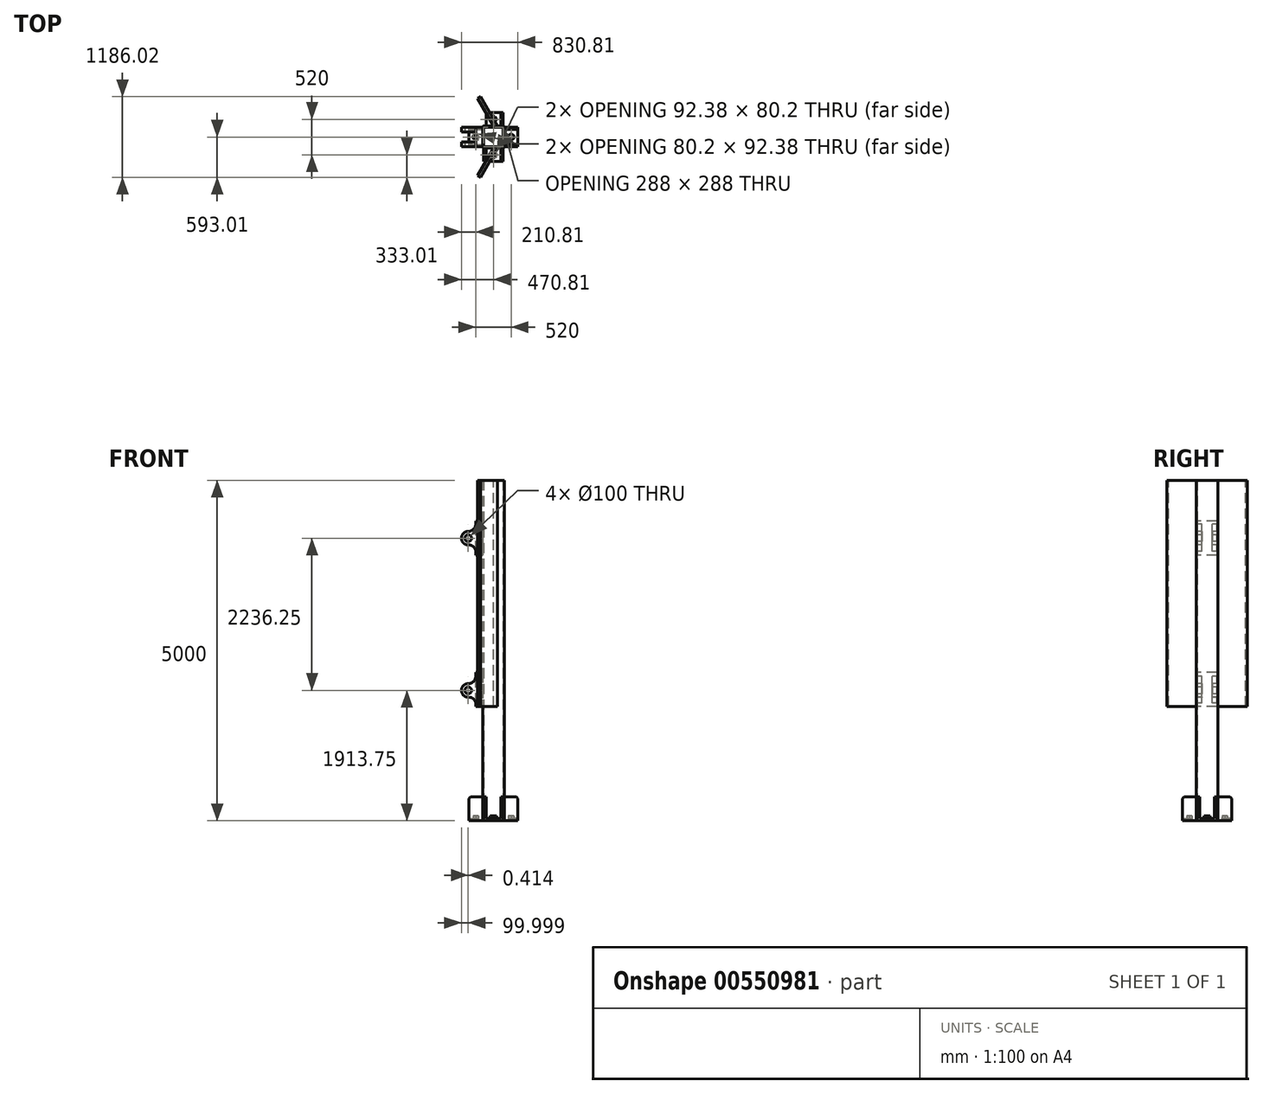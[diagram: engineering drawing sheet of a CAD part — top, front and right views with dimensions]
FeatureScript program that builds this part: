
annotation { "Feature Type Name" : "Feature", "Feature Type Description" : "" }
export const myFeature = defineFeature(function(context is Context, id is Id, definition is map)
    precondition{}
    {
        {
            var Q0;
            Q0=qCreatedBy(makeId("Top.planeOp"),FACE);
            var sketch = newSketch(context, id + "F0", { "sketchPlane" : qUnion([Q0])});
            skLineSegment(sketch, "E0.bottom", {"start": v(144, -160) * mm, "end": v(-144, -160) * mm});
            skLineSegment(sketch, "E0.top", {"start": v(144, 160) * mm, "end": v(-144, 160) * mm});
            skLineSegment(sketch, "E0.left", {"start": v(160, -144) * mm, "end": v(160, 144) * mm});
            skLineSegment(sketch, "E0.right", {"start": v(-160, -144) * mm, "end": v(-160, 144) * mm});
            skPoint(sketch, "E0.middle", {"position": v(0, 0) * mm});
            skLineSegment(sketch, "E1.0", {"start": v(128, 144) * mm, "end": v(-128, 144) * mm});
            skLineSegment(sketch, "E1.1", {"start": v(144, -128) * mm, "end": v(144, 128) * mm});
            skLineSegment(sketch, "E1.2", {"start": v(128, -144) * mm, "end": v(-128, -144) * mm});
            skLineSegment(sketch, "E1.3", {"start": v(-144, -128) * mm, "end": v(-144, 128) * mm});
            skPoint(sketch, "E2.visualSharp", {"position": v(-144, 144) * mm});
            skArc(sketch, "E2.filletArc", {"start": v(-128, 144) * mm, "mid": v(-139.31, 139.31) * mm, "end": v(-144, 128) * mm});
            skPoint(sketch, "E3.visualSharp", {"position": v(-160, 160) * mm});
            skArc(sketch, "E3.filletArc", {"start": v(-144, 160) * mm, "mid": v(-155.31, 155.31) * mm, "end": v(-160, 144) * mm});
            skPoint(sketch, "E4.visualSharp", {"position": v(-160, -160) * mm});
            skArc(sketch, "E4.filletArc", {"start": v(-160, -144) * mm, "mid": v(-155.31, -155.31) * mm, "end": v(-144, -160) * mm});
            skArc(sketch, "E5.filletArc", {"start": v(-144, -128) * mm, "mid": v(-139.31, -139.31) * mm, "end": v(-128, -144) * mm});
            skPoint(sketch, "E6.visualSharp", {"position": v(144, -144) * mm});
            skArc(sketch, "E6.filletArc", {"start": v(128, -144) * mm, "mid": v(139.31, -139.31) * mm, "end": v(144, -128) * mm});
            skPoint(sketch, "E7.visualSharp", {"position": v(160, -160) * mm});
            skArc(sketch, "E7.filletArc", {"start": v(144, -160) * mm, "mid": v(155.31, -155.31) * mm, "end": v(160, -144) * mm});
            skPoint(sketch, "E8.visualSharp", {"position": v(160, 160) * mm});
            skArc(sketch, "E8.filletArc", {"start": v(160, 144) * mm, "mid": v(155.31, 155.31) * mm, "end": v(144, 160) * mm});
            skArc(sketch, "E9.filletArc", {"start": v(144, 128) * mm, "mid": v(139.31, 139.31) * mm, "end": v(128, 144) * mm});
            skLineSegment(sketch, "E10", {"start": v(0, 0) * mm, "end": v(0, 254.28) * mm, "construction": true});
            skLineSegment(sketch, "E11.0", {"start": v(46.19, 259.8) * mm, "end": v(22.92, 219.9) * mm});
            skLineSegment(sketch, "E11.1", {"start": v(22.92, 219.9) * mm, "end": v(-23.27, 220.1) * mm});
            skLineSegment(sketch, "E11.2", {"start": v(-23.27, 220.1) * mm, "end": v(-46.19, 260.2) * mm});
            skLineSegment(sketch, "E11.3", {"start": v(-46.19, 260.2) * mm, "end": v(-22.92, 300.1) * mm});
            skLineSegment(sketch, "E11.4", {"start": v(-22.92, 300.1) * mm, "end": v(23.27, 299.9) * mm});
            skLineSegment(sketch, "E11.5", {"start": v(23.27, 299.9) * mm, "end": v(46.19, 259.8) * mm});
            skPoint(sketch, "E11.0.midPoint", {"position": v(34.55, 239.85) * mm});
            skLineSegment(sketch, "E12.bottom", {"start": v(-144, 160) * mm, "end": v(-109, 160) * mm});
            skLineSegment(sketch, "E12.top", {"start": v(-144, 360) * mm, "end": v(-109, 360) * mm});
            skLineSegment(sketch, "E12.left", {"start": v(-144, 160) * mm, "end": v(-144, 360) * mm});
            skLineSegment(sketch, "E12.right", {"start": v(144, 160) * mm, "end": v(144, 360) * mm});
            skLineSegment(sketch, "E13.1.0", {"start": v(-160, -144) * mm, "end": v(-360, -144) * mm});
            skLineSegment(sketch, "E13.1.1", {"start": v(-360, -144) * mm, "end": v(-360, 144) * mm});
            skLineSegment(sketch, "E13.1.2", {"start": v(-160, 144) * mm, "end": v(-360, 144) * mm});
            skLineSegment(sketch, "E13.1.3", {"start": v(-300.1, -22.92) * mm, "end": v(-299.9, 23.27) * mm});
            skLineSegment(sketch, "E13.1.4", {"start": v(-299.9, 23.27) * mm, "end": v(-259.8, 46.19) * mm});
            skPoint(sketch, "E13.1.5", {"position": v(-239.85, 34.55) * mm});
            skLineSegment(sketch, "E13.1.6", {"start": v(-259.8, 46.19) * mm, "end": v(-219.9, 22.92) * mm});
            skLineSegment(sketch, "E13.1.7", {"start": v(-219.9, 22.92) * mm, "end": v(-220.1, -23.27) * mm});
            skLineSegment(sketch, "E13.1.8", {"start": v(-220.1, -23.27) * mm, "end": v(-260.2, -46.19) * mm});
            skLineSegment(sketch, "E13.1.9", {"start": v(-260.2, -46.19) * mm, "end": v(-300.1, -22.92) * mm});
            skLineSegment(sketch, "E13.2.0", {"start": v(144, -160) * mm, "end": v(144, -360) * mm});
            skLineSegment(sketch, "E13.2.1", {"start": v(144, -360) * mm, "end": v(-144, -360) * mm});
            skLineSegment(sketch, "E13.2.2", {"start": v(-144, -160) * mm, "end": v(-144, -360) * mm});
            skLineSegment(sketch, "E13.2.3", {"start": v(22.92, -300.1) * mm, "end": v(-23.27, -299.9) * mm});
            skLineSegment(sketch, "E13.2.4", {"start": v(-23.27, -299.9) * mm, "end": v(-46.19, -259.8) * mm});
            skPoint(sketch, "E13.2.5", {"position": v(-34.55, -239.85) * mm});
            skLineSegment(sketch, "E13.2.6", {"start": v(-46.19, -259.8) * mm, "end": v(-22.92, -219.9) * mm});
            skLineSegment(sketch, "E13.2.7", {"start": v(-22.92, -219.9) * mm, "end": v(23.27, -220.1) * mm});
            skLineSegment(sketch, "E13.2.8", {"start": v(23.27, -220.1) * mm, "end": v(46.19, -260.2) * mm});
            skLineSegment(sketch, "E13.2.9", {"start": v(46.19, -260.2) * mm, "end": v(22.92, -300.1) * mm});
            skLineSegment(sketch, "E13.3.0", {"start": v(160, 144) * mm, "end": v(360, 144) * mm});
            skLineSegment(sketch, "E13.3.1", {"start": v(360, 144) * mm, "end": v(360, -144) * mm});
            skLineSegment(sketch, "E13.3.2", {"start": v(160, -144) * mm, "end": v(360, -144) * mm});
            skLineSegment(sketch, "E13.3.3", {"start": v(300.1, 22.92) * mm, "end": v(299.9, -23.27) * mm});
            skLineSegment(sketch, "E13.3.4", {"start": v(299.9, -23.27) * mm, "end": v(259.8, -46.19) * mm});
            skPoint(sketch, "E13.3.5", {"position": v(239.85, -34.55) * mm});
            skLineSegment(sketch, "E13.3.6", {"start": v(259.8, -46.19) * mm, "end": v(219.9, -22.92) * mm});
            skLineSegment(sketch, "E13.3.7", {"start": v(219.9, -22.92) * mm, "end": v(220.1, 23.27) * mm});
            skLineSegment(sketch, "E13.3.8", {"start": v(220.1, 23.27) * mm, "end": v(260.2, 46.19) * mm});
            skLineSegment(sketch, "E13.3.9", {"start": v(260.2, 46.19) * mm, "end": v(300.1, 22.92) * mm});
            skLineSegment(sketch, "E14", {"start": v(-109, 360) * mm, "end": v(-109, 160) * mm});
            skLineSegment(sketch, "E15", {"start": v(109, 360) * mm, "end": v(109, 160) * mm});
            skLineSegment(sketch, "E16", {"start": v(-109, 360) * mm, "end": v(109, 360) * mm});
            skLineSegment(sketch, "E17", {"start": v(109, 360) * mm, "end": v(144, 360) * mm});
            skLineSegment(sketch, "E18", {"start": v(-109, 160) * mm, "end": v(109, 160) * mm});
            skLineSegment(sketch, "E19", {"start": v(109, 160) * mm, "end": v(144, 160) * mm});
            skLineSegment(sketch, "E20.1.0", {"start": v(-360, -109) * mm, "end": v(-160, -109) * mm});
            skLineSegment(sketch, "E20.1.1", {"start": v(-360, 109) * mm, "end": v(-160, 109) * mm});
            skLineSegment(sketch, "E20.2.0", {"start": v(109, -360) * mm, "end": v(109, -160) * mm});
            skLineSegment(sketch, "E20.2.1", {"start": v(-109, -360) * mm, "end": v(-109, -160) * mm});
            skLineSegment(sketch, "E20.3.0", {"start": v(360, 109) * mm, "end": v(160, 109) * mm});
            skLineSegment(sketch, "E20.3.1", {"start": v(360, -109) * mm, "end": v(160, -109) * mm});
            skSolve(sketch);
        }
        {
            var Q0;
            Q0=makeQuery(id+"F0.imprint","IMPRINT",FACE,{"disambiguationData":[TD([[makeQuery(id+"F0.imprint","IMPRINT",EDGE,{"derivedFrom":sQuery(id+"F0.wireOp",EDGE,"E0.bottom")}),-1.0]])]});
            extrude(context, id + "F1", {"entities" : qUnion([Q0]), "depth" : 5000 * mm, "offsetDistance" : 25 * mm});
        }
        {
            var Q0;
            Q0=makeQuery(id+"F0.imprint","IMPRINT",FACE,{"disambiguationData":[TD([[makeQuery(id+"F0.imprint","IMPRINT",EDGE,{"derivedFrom":sQuery(id+"F0.wireOp",EDGE,"E14")}),1.0]])]});
            var Q1;
            {var subQ0=sQuery(id+"F0.wireOp",EDGE,"E20.3.0");Q1=makeQuery(id+"F0.imprint","IMPRINT",FACE,{"disambiguationData":[TD([[makeQuery(id+"F0.imprint","IMPRINT",EDGE,{"derivedFrom":subQ0}),1.0]])]});}
            var Q2;
            {var subQ0=sQuery(id+"F0.wireOp",EDGE,"E20.2.0");Q2=makeQuery(id+"F0.imprint","IMPRINT",FACE,{"disambiguationData":[TD([[makeQuery(id+"F0.imprint","IMPRINT",EDGE,{"derivedFrom":subQ0}),1.0]])]});}
            var Q3;
            {var subQ0=sQuery(id+"F0.wireOp",EDGE,"E20.1.0");Q3=makeQuery(id+"F0.imprint","IMPRINT",FACE,{"disambiguationData":[TD([[makeQuery(id+"F0.imprint","IMPRINT",EDGE,{"derivedFrom":subQ0}),1.0]])]});}
            extrude(context, id + "F2", {"entities" : qUnion([Q0, Q1, Q2, Q3]), "operationType" : NewBodyOperationType.ADD, "depth" : 35 * mm, "offsetDistance" : 25 * mm});
        }
        {
            var Q0;
            Q0=makeQuery(id+"F0.imprint","IMPRINT",FACE,{"disambiguationData":[TD([[makeQuery(id+"F0.imprint","IMPRINT",EDGE,{"derivedFrom":sQuery(id+"F0.wireOp",EDGE,"E12.bottom")}),1.0]])]});
            var Q1;
            Q1=makeQuery(id+"F0.imprint","IMPRINT",FACE,{"disambiguationData":[TD([[makeQuery(id+"F0.imprint","IMPRINT",EDGE,{"derivedFrom":sQuery(id+"F0.wireOp",EDGE,"E12.right")}),1.0]])]});
            var Q2;
            {var subQ0=sQuery(id+"F0.wireOp",EDGE,"E13.3.0");Q2=makeQuery(id+"F0.imprint","IMPRINT",FACE,{"disambiguationData":[TD([[makeQuery(id+"F0.imprint","IMPRINT",EDGE,{"derivedFrom":subQ0}),-1.0]])]});}
            var Q3;
            {var subQ0=sQuery(id+"F0.wireOp",EDGE,"E13.3.2");Q3=makeQuery(id+"F0.imprint","IMPRINT",FACE,{"disambiguationData":[TD([[makeQuery(id+"F0.imprint","IMPRINT",EDGE,{"derivedFrom":subQ0}),1.0]])]});}
            var Q4;
            {var subQ0=sQuery(id+"F0.wireOp",EDGE,"E13.2.0");Q4=makeQuery(id+"F0.imprint","IMPRINT",FACE,{"disambiguationData":[TD([[makeQuery(id+"F0.imprint","IMPRINT",EDGE,{"derivedFrom":subQ0}),-1.0]])]});}
            var Q5;
            {var subQ0=sQuery(id+"F0.wireOp",EDGE,"E13.1.0");Q5=makeQuery(id+"F0.imprint","IMPRINT",FACE,{"disambiguationData":[TD([[makeQuery(id+"F0.imprint","IMPRINT",EDGE,{"derivedFrom":subQ0}),-1.0]])]});}
            var Q6;
            {var subQ0=sQuery(id+"F0.wireOp",EDGE,"E13.1.2");Q6=makeQuery(id+"F0.imprint","IMPRINT",FACE,{"disambiguationData":[TD([[makeQuery(id+"F0.imprint","IMPRINT",EDGE,{"derivedFrom":subQ0}),1.0]])]});}
            var Q7;
            {var subQ0=sQuery(id+"F0.wireOp",EDGE,"E13.2.2");Q7=makeQuery(id+"F0.imprint","IMPRINT",FACE,{"disambiguationData":[TD([[makeQuery(id+"F0.imprint","IMPRINT",EDGE,{"derivedFrom":subQ0}),1.0]])]});}
            extrude(context, id + "F3", {"entities" : qUnion([Q0, Q1, Q2, Q3, Q4, Q5, Q6, Q7]), "operationType" : NewBodyOperationType.ADD, "depth" : 350 * mm, "offsetDistance" : 25 * mm});
        }
        {
            var Q0;
            Q0=makeQuery(id+"F0.imprint","IMPRINT",FACE,{"disambiguationData":[TD([[makeQuery(id+"F0.imprint","IMPRINT",EDGE,{"derivedFrom":sQuery(id+"F0.wireOp",EDGE,"E13.1.3")}),-1.0]])]});
            var Q1;
            Q1=makeQuery(id+"F0.imprint","IMPRINT",FACE,{"disambiguationData":[TD([[makeQuery(id+"F0.imprint","IMPRINT",EDGE,{"derivedFrom":sQuery(id+"F0.wireOp",EDGE,"E13.2.3")}),-1.0]])]});
            var Q2;
            Q2=makeQuery(id+"F0.imprint","IMPRINT",FACE,{"disambiguationData":[TD([[makeQuery(id+"F0.imprint","IMPRINT",EDGE,{"derivedFrom":sQuery(id+"F0.wireOp",EDGE,"E13.3.3")}),-1.0]])]});
            var Q3;
            Q3=makeQuery(id+"F0.imprint","IMPRINT",FACE,{"disambiguationData":[TD([[makeQuery(id+"F0.imprint","IMPRINT",EDGE,{"derivedFrom":sQuery(id+"F0.wireOp",EDGE,"E11.0")}),-1.0]])]});
            var Q4;
            Q4=makeQuery(id+"F2.opExtrude","CAP_FACE",FACE,{"disambiguationData":[OSD([sQuery(id+"F0.wireOp",EDGE,"E11.0"),sQuery(id+"F0.wireOp",EDGE,"E11.1"),sQuery(id+"F0.wireOp",EDGE,"E11.2"),sQuery(id+"F0.wireOp",EDGE,"E11.3"),sQuery(id+"F0.wireOp",EDGE,"E11.4"),sQuery(id+"F0.wireOp",EDGE,"E11.5"),sQuery(id+"F0.wireOp",EDGE,"E14"),sQuery(id+"F0.wireOp",EDGE,"E15"),sQuery(id+"F0.wireOp",EDGE,"E16"),sQuery(id+"F0.wireOp",EDGE,"E18")])],"isStart":false});
            extrude(context, id + "F4", {"entities" : qUnion([Q0, Q1, Q2, Q3]), "endBound" : BoundingType.UP_TO_SURFACE, "depth" : 25 * mm, "endBoundEntityFace" : qUnion([Q4]), "hasOffset" : true, "offsetDistance" : 35 * mm, "offsetOppositeDirection" : true});
        }
        {
            var Q0;
            {var subQ0=sQuery(id+"F0.wireOp",EDGE,"E13.2.1");Q0=makeQuery(id+"F3.opExtrude","CAP_EDGE",EDGE,{"disambiguationData":[OSD([subQ0]),TDD([makeQuery(id+"F0.imprint","IMPRINT",EDGE,{"disambiguationData":[TD([[makeQuery(id+"F0.imprint","INTERSECT",VERTEX,{"derivedFrom":[sQuery(id+"F0.wireOp",EDGE,"E13.2.0"),subQ0]}),-1.0]])],"derivedFrom":subQ0})])],"isStart":false});}
            var Q1;
            {var subQ0=sQuery(id+"F0.wireOp",EDGE,"E13.2.1");Q1=makeQuery(id+"F3.opExtrude","CAP_EDGE",EDGE,{"disambiguationData":[OSD([subQ0]),TDD([makeQuery(id+"F0.imprint","IMPRINT",EDGE,{"disambiguationData":[TD([[makeQuery(id+"F0.imprint","INTERSECT",VERTEX,{"derivedFrom":[subQ0,sQuery(id+"F0.wireOp",EDGE,"E13.2.2")]}),1.0]])],"derivedFrom":subQ0})])],"isStart":false});}
            var Q2;
            {var subQ0=sQuery(id+"F0.wireOp",EDGE,"E13.1.1");Q2=makeQuery(id+"F3.opExtrude","CAP_EDGE",EDGE,{"disambiguationData":[OSD([subQ0]),TDD([makeQuery(id+"F0.imprint","IMPRINT",EDGE,{"disambiguationData":[TD([[makeQuery(id+"F0.imprint","INTERSECT",VERTEX,{"derivedFrom":[subQ0,sQuery(id+"F0.wireOp",EDGE,"E13.1.2")]}),1.0]])],"derivedFrom":subQ0})])],"isStart":false});}
            var Q3;
            {var subQ0=sQuery(id+"F0.wireOp",EDGE,"E13.1.1");Q3=makeQuery(id+"F3.opExtrude","CAP_EDGE",EDGE,{"disambiguationData":[OSD([subQ0]),TDD([makeQuery(id+"F0.imprint","IMPRINT",EDGE,{"disambiguationData":[TD([[makeQuery(id+"F0.imprint","INTERSECT",VERTEX,{"derivedFrom":[sQuery(id+"F0.wireOp",EDGE,"E13.1.0"),subQ0]}),-1.0]])],"derivedFrom":subQ0})])],"isStart":false});}
            var Q4;
            Q4=makeQuery(id+"F3.opExtrude","CAP_EDGE",EDGE,{"disambiguationData":[OSD([sQuery(id+"F0.wireOp",EDGE,"E17")])],"isStart":false});
            var Q5;
            Q5=makeQuery(id+"F3.opExtrude","CAP_EDGE",EDGE,{"disambiguationData":[OSD([sQuery(id+"F0.wireOp",EDGE,"E12.top")])],"isStart":false});
            var Q6;
            {var subQ0=sQuery(id+"F0.wireOp",EDGE,"E13.3.1");Q6=makeQuery(id+"F3.opExtrude","CAP_EDGE",EDGE,{"disambiguationData":[OSD([subQ0]),TDD([makeQuery(id+"F0.imprint","IMPRINT",EDGE,{"disambiguationData":[TD([[makeQuery(id+"F0.imprint","INTERSECT",VERTEX,{"derivedFrom":[subQ0,sQuery(id+"F0.wireOp",EDGE,"E13.3.2")]}),1.0]])],"derivedFrom":subQ0})])],"isStart":false});}
            var Q7;
            {var subQ0=sQuery(id+"F0.wireOp",EDGE,"E13.3.1");Q7=makeQuery(id+"F3.opExtrude","CAP_EDGE",EDGE,{"disambiguationData":[OSD([subQ0]),TDD([makeQuery(id+"F0.imprint","IMPRINT",EDGE,{"disambiguationData":[TD([[makeQuery(id+"F0.imprint","INTERSECT",VERTEX,{"derivedFrom":[sQuery(id+"F0.wireOp",EDGE,"E13.3.0"),subQ0]}),-1.0]])],"derivedFrom":subQ0})])],"isStart":false});}
            chamfer(context, id + "F5", {"entities" : qUnion([Q0, Q1, Q2, Q3, Q4, Q5, Q6, Q7]), "width" : 25 * mm, "tangentPropagation" : true});
        }
        {
            var Q0;
            Q0=makeQuery(id+"F3.opExtrude","SWEPT_EDGE",EDGE,{"disambiguationData":[OSD([sQuery(id+"F0.wireOp",EDGE,"E0.left"),sQuery(id+"F0.wireOp",EDGE,"E20.3.1")])]});
            var Q1;
            Q1=makeQuery(id+"F3.opExtrude","SWEPT_EDGE",EDGE,{"disambiguationData":[OSD([sQuery(id+"F0.wireOp",EDGE,"E12.bottom"),sQuery(id+"F0.wireOp",EDGE,"E14"),sQuery(id+"F0.wireOp",EDGE,"E18")])]});
            var Q2;
            Q2=makeQuery(id+"F3.opExtrude","SWEPT_EDGE",EDGE,{"disambiguationData":[OSD([sQuery(id+"F0.wireOp",EDGE,"E0.left"),sQuery(id+"F0.wireOp",EDGE,"E20.3.0")])]});
            var Q3;
            Q3=makeQuery(id+"F3.opExtrude","SWEPT_EDGE",EDGE,{"disambiguationData":[OSD([sQuery(id+"F0.wireOp",EDGE,"E0.bottom"),sQuery(id+"F0.wireOp",EDGE,"E20.2.1")])]});
            var Q4;
            Q4=makeQuery(id+"F3.opExtrude","SWEPT_EDGE",EDGE,{"disambiguationData":[OSD([sQuery(id+"F0.wireOp",EDGE,"E0.bottom"),sQuery(id+"F0.wireOp",EDGE,"E20.2.0")])]});
            var Q5;
            Q5=makeQuery(id+"F3.opExtrude","SWEPT_EDGE",EDGE,{"disambiguationData":[OSD([sQuery(id+"F0.wireOp",EDGE,"E0.right"),sQuery(id+"F0.wireOp",EDGE,"E20.1.0")])]});
            var Q6;
            Q6=makeQuery(id+"F3.opExtrude","SWEPT_EDGE",EDGE,{"disambiguationData":[OSD([sQuery(id+"F0.wireOp",EDGE,"E15"),sQuery(id+"F0.wireOp",EDGE,"E18"),sQuery(id+"F0.wireOp",EDGE,"E19")])]});
            var Q7;
            Q7=makeQuery(id+"F3.opExtrude","SWEPT_EDGE",EDGE,{"disambiguationData":[OSD([sQuery(id+"F0.wireOp",EDGE,"E0.right"),sQuery(id+"F0.wireOp",EDGE,"E20.1.1")])]});
            var Q8;
            Q8=makeQuery(id+"F2.opExtrude","CAP_EDGE",EDGE,{"disambiguationData":[OSD([sQuery(id+"F0.wireOp",EDGE,"E20.1.1")])],"isStart":false});
            var Q9;
            Q9=makeQuery(id+"F2.opExtrude","CAP_EDGE",EDGE,{"disambiguationData":[OSD([sQuery(id+"F0.wireOp",EDGE,"E20.1.0")])],"isStart":false});
            var Q10;
            Q10=makeQuery(id+"F2.opExtrude","CAP_EDGE",EDGE,{"disambiguationData":[OSD([sQuery(id+"F0.wireOp",EDGE,"E14")])],"isStart":false});
            var Q11;
            Q11=makeQuery(id+"F2.opExtrude","CAP_EDGE",EDGE,{"disambiguationData":[OSD([sQuery(id+"F0.wireOp",EDGE,"E18")])],"isStart":false});
            var Q12;
            Q12=makeQuery(id+"F2.opExtrude","CAP_EDGE",EDGE,{"disambiguationData":[OSD([sQuery(id+"F0.wireOp",EDGE,"E15")])],"isStart":false});
            var Q13;
            Q13=makeQuery(id+"F2.opExtrude","CAP_EDGE",EDGE,{"disambiguationData":[OSD([sQuery(id+"F0.wireOp",EDGE,"E20.3.0")])],"isStart":false});
            var Q14;
            Q14=makeQuery(id+"F2.opExtrude","CAP_EDGE",EDGE,{"disambiguationData":[OSD([sQuery(id+"F0.wireOp",EDGE,"E0.left")])],"isStart":false});
            var Q15;
            Q15=makeQuery(id+"F2.opExtrude","CAP_EDGE",EDGE,{"disambiguationData":[OSD([sQuery(id+"F0.wireOp",EDGE,"E20.3.1")])],"isStart":false});
            var Q16;
            Q16=makeQuery(id+"F2.opExtrude","CAP_EDGE",EDGE,{"disambiguationData":[OSD([sQuery(id+"F0.wireOp",EDGE,"E20.2.0")])],"isStart":false});
            var Q17;
            Q17=makeQuery(id+"F2.opExtrude","CAP_EDGE",EDGE,{"disambiguationData":[OSD([sQuery(id+"F0.wireOp",EDGE,"E0.bottom")])],"isStart":false});
            var Q18;
            Q18=makeQuery(id+"F2.opExtrude","CAP_EDGE",EDGE,{"disambiguationData":[OSD([sQuery(id+"F0.wireOp",EDGE,"E20.2.1")])],"isStart":false});
            var Q19;
            {var subQ0=sQuery(id+"F0.wireOp",EDGE,"E0.bottom");Q19=makeQuery(id+"F3.opExtrude","CAP_EDGE",EDGE,{"disambiguationData":[OSD([subQ0]),TDD([makeQuery(id+"F0.imprint","IMPRINT",EDGE,{"disambiguationData":[TD([[makeQuery(id+"F0.imprint","INTERSECT",VERTEX,{"derivedFrom":[subQ0,sQuery(id+"F0.wireOp",EDGE,"E20.2.1")]}),-1.0]])],"derivedFrom":subQ0})])],"isStart":false});}
            var Q20;
            {var subQ0=sQuery(id+"F0.wireOp",EDGE,"E0.bottom");Q20=makeQuery(id+"F3.opExtrude","CAP_EDGE",EDGE,{"disambiguationData":[OSD([subQ0]),TDD([makeQuery(id+"F0.imprint","IMPRINT",EDGE,{"disambiguationData":[TD([[makeQuery(id+"F0.imprint","INTERSECT",VERTEX,{"derivedFrom":[subQ0,sQuery(id+"F0.wireOp",EDGE,"E20.2.0")]}),1.0]])],"derivedFrom":subQ0})])],"isStart":false});}
            var Q21;
            {var subQ0=sQuery(id+"F0.wireOp",EDGE,"E0.left");Q21=makeQuery(id+"F3.opExtrude","CAP_EDGE",EDGE,{"disambiguationData":[OSD([subQ0]),TDD([makeQuery(id+"F0.imprint","IMPRINT",EDGE,{"disambiguationData":[TD([[makeQuery(id+"F0.imprint","INTERSECT",VERTEX,{"derivedFrom":[subQ0,sQuery(id+"F0.wireOp",EDGE,"E20.3.1")]}),1.0]])],"derivedFrom":subQ0})])],"isStart":false});}
            var Q22;
            {var subQ0=sQuery(id+"F0.wireOp",EDGE,"E0.left");Q22=makeQuery(id+"F3.opExtrude","CAP_EDGE",EDGE,{"disambiguationData":[OSD([subQ0]),TDD([makeQuery(id+"F0.imprint","IMPRINT",EDGE,{"disambiguationData":[TD([[makeQuery(id+"F0.imprint","INTERSECT",VERTEX,{"derivedFrom":[subQ0,sQuery(id+"F0.wireOp",EDGE,"E20.3.0")]}),-1.0]])],"derivedFrom":subQ0})])],"isStart":false});}
            var Q23;
            Q23=makeQuery(id+"F3.opExtrude","CAP_EDGE",EDGE,{"disambiguationData":[OSD([sQuery(id+"F0.wireOp",EDGE,"E19")])],"isStart":false});
            var Q24;
            Q24=makeQuery(id+"F3.opExtrude","CAP_EDGE",EDGE,{"disambiguationData":[OSD([sQuery(id+"F0.wireOp",EDGE,"E12.bottom")])],"isStart":false});
            var Q25;
            {var subQ0=sQuery(id+"F0.wireOp",EDGE,"E0.right");Q25=makeQuery(id+"F3.opExtrude","CAP_EDGE",EDGE,{"disambiguationData":[OSD([subQ0]),TDD([makeQuery(id+"F0.imprint","IMPRINT",EDGE,{"disambiguationData":[TD([[makeQuery(id+"F0.imprint","INTERSECT",VERTEX,{"derivedFrom":[subQ0,sQuery(id+"F0.wireOp",EDGE,"E20.1.1")]}),-1.0]])],"derivedFrom":subQ0})])],"isStart":false});}
            var Q26;
            {var subQ0=sQuery(id+"F0.wireOp",EDGE,"E0.right");Q26=makeQuery(id+"F3.opExtrude","CAP_EDGE",EDGE,{"disambiguationData":[OSD([subQ0]),TDD([makeQuery(id+"F0.imprint","IMPRINT",EDGE,{"disambiguationData":[TD([[makeQuery(id+"F0.imprint","INTERSECT",VERTEX,{"derivedFrom":[subQ0,sQuery(id+"F0.wireOp",EDGE,"E20.1.0")]}),1.0]])],"derivedFrom":subQ0})])],"isStart":false});}
            fillet(context, id + "F6", {"entities" : qUnion([Q0, Q1, Q2, Q3, Q4, Q5, Q6, Q7, Q8, Q9, Q10, Q11, Q12, Q13, Q14, Q15, Q16, Q17, Q18, Q19, Q20, Q21, Q22, Q23, Q24, Q25, Q26]), "radius" : 15 * mm, "tangentPropagation" : true, "allowEdgeOverflow" : false});
        }
        {
            var Q0;
            Q0=makeQuery(id+"F1.opExtrude","SWEPT_FACE",FACE,{"disambiguationData":[OSD([sQuery(id+"F0.wireOp",EDGE,"E0.right")])]});
            var sketch = newSketch(context, id + "F7", { "sketchPlane" : qUnion([Q0])});
            skLineSegment(sketch, "E21.0", {"start": v(128, 5000) * mm, "end": v(-128, 5000) * mm, "construction": true});
            skLineSegment(sketch, "E21.1", {"start": v(128, 0) * mm, "end": v(-128, 0) * mm, "construction": true});
            skLineSegment(sketch, "E22", {"start": v(-144, 1927) * mm, "end": v(144, 1927) * mm});
            skLineSegment(sketch, "E23", {"start": v(-144, 4150) * mm, "end": v(144, 4150) * mm});
            skLineSegment(sketch, "E24.bottom", {"start": v(-144, 3900) * mm, "end": v(144, 3900) * mm});
            skLineSegment(sketch, "E24.top", {"start": v(-144, 4400) * mm, "end": v(144, 4400) * mm});
            skLineSegment(sketch, "E24.left", {"start": v(-144, 3900) * mm, "end": v(-144, 4400) * mm});
            skLineSegment(sketch, "E24.right", {"start": v(144, 3900) * mm, "end": v(144, 4400) * mm});
            skPoint(sketch, "E24.middle", {"position": v(0, 4150) * mm});
            skLineSegment(sketch, "E25.bottom", {"start": v(-144, 1677) * mm, "end": v(144, 1677) * mm});
            skLineSegment(sketch, "E25.top", {"start": v(-144, 2177) * mm, "end": v(144, 2177) * mm});
            skLineSegment(sketch, "E25.left", {"start": v(-144, 1677) * mm, "end": v(-144, 2177) * mm});
            skLineSegment(sketch, "E25.right", {"start": v(144, 1677) * mm, "end": v(144, 2177) * mm});
            skPoint(sketch, "E25.middle", {"position": v(0, 1927) * mm});
            skLineSegment(sketch, "E26", {"start": v(44, 4400) * mm, "end": v(44, 3900) * mm});
            skLineSegment(sketch, "E27", {"start": v(-44, 4400) * mm, "end": v(-44, 3900) * mm});
            skLineSegment(sketch, "E28.trimOffspring", {"start": v(44, 2177) * mm, "end": v(44, 1677) * mm});
            skLineSegment(sketch, "E29.trimOffspring", {"start": v(-44, 2177) * mm, "end": v(-44, 1677) * mm});
            skSolve(sketch);
        }
        {
            var Q0;
            {var subQ0=sQuery(id+"F7.wireOp",EDGE,"E24.left");var subQ1=sQuery(id+"F7.wireOp",EDGE,"E23");var subQ2=makeQuery(id+"F7.imprint","INTERSECT",VERTEX,{"derivedFrom":[subQ1,subQ0]});Q0=makeQuery(id+"F7.imprint","IMPRINT",FACE,{"disambiguationData":[TD([[makeQuery(id+"F7.imprint","IMPRINT",EDGE,{"disambiguationData":[TD([[subQ2,-1.0]])],"derivedFrom":subQ1}),1.0]])]});}
            var Q1;
            {var subQ0=sQuery(id+"F7.wireOp",EDGE,"E24.left");var subQ1=sQuery(id+"F7.wireOp",EDGE,"E23");var subQ2=makeQuery(id+"F7.imprint","INTERSECT",VERTEX,{"derivedFrom":[subQ1,subQ0]});Q1=makeQuery(id+"F7.imprint","IMPRINT",FACE,{"disambiguationData":[TD([[makeQuery(id+"F7.imprint","IMPRINT",EDGE,{"disambiguationData":[TD([[subQ2,-1.0]])],"derivedFrom":subQ1}),-1.0]])]});}
            var Q2;
            {var subQ0=sQuery(id+"F7.wireOp",EDGE,"E24.right");var subQ1=sQuery(id+"F7.wireOp",EDGE,"E23");var subQ2=makeQuery(id+"F7.imprint","INTERSECT",VERTEX,{"derivedFrom":[subQ1,subQ0]});Q2=makeQuery(id+"F7.imprint","IMPRINT",FACE,{"disambiguationData":[TD([[makeQuery(id+"F7.imprint","IMPRINT",EDGE,{"disambiguationData":[TD([[subQ2,1.0]])],"derivedFrom":subQ1}),1.0]])]});}
            var Q3;
            {var subQ0=sQuery(id+"F7.wireOp",EDGE,"E24.right");var subQ1=sQuery(id+"F7.wireOp",EDGE,"E23");var subQ2=makeQuery(id+"F7.imprint","INTERSECT",VERTEX,{"derivedFrom":[subQ1,subQ0]});Q3=makeQuery(id+"F7.imprint","IMPRINT",FACE,{"disambiguationData":[TD([[makeQuery(id+"F7.imprint","IMPRINT",EDGE,{"disambiguationData":[TD([[subQ2,1.0]])],"derivedFrom":subQ1}),-1.0]])]});}
            var Q4;
            {var subQ0=sQuery(id+"F7.wireOp",EDGE,"E25.left");var subQ1=sQuery(id+"F7.wireOp",EDGE,"E22");var subQ2=makeQuery(id+"F7.imprint","INTERSECT",VERTEX,{"derivedFrom":[subQ1,subQ0]});Q4=makeQuery(id+"F7.imprint","IMPRINT",FACE,{"disambiguationData":[TD([[makeQuery(id+"F7.imprint","IMPRINT",EDGE,{"disambiguationData":[TD([[subQ2,-1.0]])],"derivedFrom":subQ1}),1.0]])]});}
            var Q5;
            {var subQ0=sQuery(id+"F7.wireOp",EDGE,"E25.left");var subQ1=sQuery(id+"F7.wireOp",EDGE,"E22");var subQ2=makeQuery(id+"F7.imprint","INTERSECT",VERTEX,{"derivedFrom":[subQ1,subQ0]});Q5=makeQuery(id+"F7.imprint","IMPRINT",FACE,{"disambiguationData":[TD([[makeQuery(id+"F7.imprint","IMPRINT",EDGE,{"disambiguationData":[TD([[subQ2,-1.0]])],"derivedFrom":subQ1}),-1.0]])]});}
            var Q6;
            {var subQ0=sQuery(id+"F7.wireOp",EDGE,"E25.right");var subQ1=sQuery(id+"F7.wireOp",EDGE,"E22");var subQ2=makeQuery(id+"F7.imprint","INTERSECT",VERTEX,{"derivedFrom":[subQ1,subQ0]});Q6=makeQuery(id+"F7.imprint","IMPRINT",FACE,{"disambiguationData":[TD([[makeQuery(id+"F7.imprint","IMPRINT",EDGE,{"disambiguationData":[TD([[subQ2,1.0]])],"derivedFrom":subQ1}),1.0]])]});}
            var Q7;
            {var subQ0=sQuery(id+"F7.wireOp",EDGE,"E25.right");var subQ1=sQuery(id+"F7.wireOp",EDGE,"E22");var subQ2=makeQuery(id+"F7.imprint","INTERSECT",VERTEX,{"derivedFrom":[subQ1,subQ0]});Q7=makeQuery(id+"F7.imprint","IMPRINT",FACE,{"disambiguationData":[TD([[makeQuery(id+"F7.imprint","IMPRINT",EDGE,{"disambiguationData":[TD([[subQ2,1.0]])],"derivedFrom":subQ1}),-1.0]])]});}
            var Q8;
            {var subQ0=sQuery(id+"F7.wireOp",EDGE,"E27");var subQ1=sQuery(id+"F7.wireOp",EDGE,"E23");var subQ2=makeQuery(id+"F7.imprint","INTERSECT",VERTEX,{"derivedFrom":[subQ1,subQ0]});Q8=makeQuery(id+"F7.imprint","IMPRINT",FACE,{"disambiguationData":[TD([[makeQuery(id+"F7.imprint","IMPRINT",EDGE,{"disambiguationData":[TD([[subQ2,-1.0]])],"derivedFrom":subQ1}),1.0]])]});}
            var Q9;
            {var subQ0=sQuery(id+"F7.wireOp",EDGE,"E27");var subQ1=sQuery(id+"F7.wireOp",EDGE,"E23");var subQ2=makeQuery(id+"F7.imprint","INTERSECT",VERTEX,{"derivedFrom":[subQ1,subQ0]});Q9=makeQuery(id+"F7.imprint","IMPRINT",FACE,{"disambiguationData":[TD([[makeQuery(id+"F7.imprint","IMPRINT",EDGE,{"disambiguationData":[TD([[subQ2,-1.0]])],"derivedFrom":subQ1}),-1.0]])]});}
            var Q10;
            {var subQ0=sQuery(id+"F7.wireOp",EDGE,"E29.trimOffspring");var subQ1=sQuery(id+"F7.wireOp",EDGE,"E22");var subQ2=makeQuery(id+"F7.imprint","INTERSECT",VERTEX,{"derivedFrom":[subQ1,subQ0]});Q10=makeQuery(id+"F7.imprint","IMPRINT",FACE,{"disambiguationData":[TD([[makeQuery(id+"F7.imprint","IMPRINT",EDGE,{"disambiguationData":[TD([[subQ2,-1.0]])],"derivedFrom":subQ1}),1.0]])]});}
            var Q11;
            {var subQ0=sQuery(id+"F7.wireOp",EDGE,"E29.trimOffspring");var subQ1=sQuery(id+"F7.wireOp",EDGE,"E22");var subQ2=makeQuery(id+"F7.imprint","INTERSECT",VERTEX,{"derivedFrom":[subQ1,subQ0]});Q11=makeQuery(id+"F7.imprint","IMPRINT",FACE,{"disambiguationData":[TD([[makeQuery(id+"F7.imprint","IMPRINT",EDGE,{"disambiguationData":[TD([[subQ2,-1.0]])],"derivedFrom":subQ1}),-1.0]])]});}
            extrude(context, id + "F8", {"entities" : qUnion([Q0, Q1, Q2, Q3, Q4, Q5, Q6, Q7, Q8, Q9, Q10, Q11]), "depth" : 100 * mm, "offsetDistance" : 25 * mm});
        }
        {
            var Q0;
            Q0=makeQuery(id+"F8.opExtrude","SWEPT_FACE",FACE,{"disambiguationData":[OSD([sQuery(id+"F7.wireOp",EDGE,"E24.right")])]});
            var sketch = newSketch(context, id + "F9", { "sketchPlane" : qUnion([Q0])});
            skLineSegment(sketch, "E30", {"start": v(-260, 4150) * mm, "end": v(-481.62, 4150) * mm});
            skCircle(sketch, "E31", {"center": v(-370.81, 4150) * mm, "radius": 50 * mm});
            skArc(sketch, "E32", {"start": v(-470.81, 4150) * mm, "mid": v(-439.75, 4077.56) * mm, "end": v(-365.87, 4050.12) * mm});
            skArc(sketch, "E33", {"start": v(-370.13, 4250) * mm, "mid": v(-441.28, 4220.95) * mm, "end": v(-470.81, 4150) * mm});
            skArc(sketch, "E34", {"start": v(-365.87, 4050.12) * mm, "mid": v(-270.83, 4152.13) * mm, "end": v(-370.13, 4250) * mm});
            skArc(sketch, "E35", {"start": v(-370.13, 4250) * mm, "mid": v(-294.19, 4279.9) * mm, "end": v(-260, 4354) * mm});
            skArc(sketch, "E36", {"start": v(-365.87, 4050.12) * mm, "mid": v(-287.25, 4018.58) * mm, "end": v(-260, 3938.37) * mm});
            skLineSegment(sketch, "E37", {"start": v(-259.59, 1913.75) * mm, "end": v(-481.2, 1913.75) * mm});
            skCircle(sketch, "E38", {"center": v(-370.4, 1913.75) * mm, "radius": 50 * mm});
            skArc(sketch, "E39", {"start": v(-470.4, 1913.75) * mm, "mid": v(-439.34, 1841.32) * mm, "end": v(-365.46, 1813.87) * mm});
            skArc(sketch, "E40", {"start": v(-369.94, 2013.75) * mm, "mid": v(-440.95, 1984.62) * mm, "end": v(-470.4, 1913.75) * mm});
            skArc(sketch, "E41", {"start": v(-365.46, 1813.87) * mm, "mid": v(-270.42, 1916) * mm, "end": v(-369.94, 2013.75) * mm});
            skArc(sketch, "E42", {"start": v(-365.46, 1813.87) * mm, "mid": v(-286.24, 1781.7) * mm, "end": v(-259.78, 1700.39) * mm});
            skLineSegment(sketch, "E43.0", {"start": v(-260, 2177) * mm, "end": v(-260, 2127.53) * mm});
            skLineSegment(sketch, "E44", {"start": v(-260, 2127.53) * mm, "end": v(-260, 1913.75) * mm});
            skLineSegment(sketch, "E45", {"start": v(-260, 1913.75) * mm, "end": v(-260, 1726.47) * mm});
            skLineSegment(sketch, "E46", {"start": v(-260, 1726.47) * mm, "end": v(-260, 1677) * mm});
            skArc(sketch, "E47", {"start": v(-369.94, 2013.75) * mm, "mid": v(-290.68, 2047.17) * mm, "end": v(-260, 2127.53) * mm});
            skSolve(sketch);
        }
        {
            var Q0;
            {var subQ5=sQuery(id+"F9.wireOp",EDGE,"E35");Q0=makeQuery(id+"F9.imprint","IMPRINT",FACE,{"disambiguationData":[TD([[makeQuery(id+"F9.imprint","IMPRINT",EDGE,{"derivedFrom":subQ5}),-1.0]])]});}
            var Q1;
            {var subQ0=sQuery(id+"F9.wireOp",EDGE,"E33");Q1=makeQuery(id+"F9.imprint","IMPRINT",FACE,{"disambiguationData":[TD([[makeQuery(id+"F9.imprint","IMPRINT",EDGE,{"derivedFrom":subQ0}),1.0]])]});}
            var Q2;
            {var subQ4=sQuery(id+"F9.wireOp",EDGE,"E32");Q2=makeQuery(id+"F9.imprint","IMPRINT",FACE,{"disambiguationData":[TD([[makeQuery(id+"F9.imprint","IMPRINT",EDGE,{"derivedFrom":subQ4}),1.0]])]});}
            var Q3;
            {var subQ0=sQuery(id+"F9.wireOp",EDGE,"E30");var subQ1=makeQuery(id+"F8.opExtrude","CAP_EDGE",EDGE,{"disambiguationData":[OSD([sQuery(id+"F7.wireOp",EDGE,"E24.right")])],"isStart":false});var subQ2=makeQuery(id+"F9.imprint","INTERSECT",VERTEX,{"derivedFrom":[subQ1,subQ0]});Q3=makeQuery(id+"F9.imprint","IMPRINT",FACE,{"disambiguationData":[TD([[makeQuery(id+"F9.imprint","IMPRINT",EDGE,{"disambiguationData":[TD([[subQ2,-1.0]])],"derivedFrom":subQ0}),1.0]])]});}
            var Q4;
            {var subQ0=sQuery(id+"F9.wireOp",EDGE,"E40");Q4=makeQuery(id+"F9.imprint","IMPRINT",FACE,{"disambiguationData":[TD([[makeQuery(id+"F9.imprint","IMPRINT",EDGE,{"derivedFrom":subQ0}),1.0]])]});}
            var Q5;
            {var subQ4=sQuery(id+"F9.wireOp",EDGE,"E39");Q5=makeQuery(id+"F9.imprint","IMPRINT",FACE,{"disambiguationData":[TD([[makeQuery(id+"F9.imprint","IMPRINT",EDGE,{"derivedFrom":subQ4}),1.0]])]});}
            var Q6;
            {var subQ0=sQuery(id+"F9.wireOp",EDGE,"E45");Q6=makeQuery(id+"F9.imprint","IMPRINT",FACE,{"disambiguationData":[TD([[makeQuery(id+"F9.imprint","IMPRINT",EDGE,{"derivedFrom":subQ0}),-1.0]])]});}
            var Q7;
            {var subQ1=sQuery(id+"F9.wireOp",EDGE,"E37");var subQ3=sQuery(id+"F9.wireOp",EDGE,"E41");var subQ4=makeQuery(id+"F9.imprint","INTERSECT",VERTEX,{"derivedFrom":[subQ1,subQ3]});Q7=makeQuery(id+"F9.imprint","IMPRINT",FACE,{"disambiguationData":[TD([[makeQuery(id+"F9.imprint","IMPRINT",EDGE,{"disambiguationData":[TD([[subQ4,1.0]])],"derivedFrom":subQ1}),-1.0]])]});}
            var Q8;
            Q8=makeQuery(id+"F8.opExtrude","SWEPT_FACE",FACE,{"disambiguationData":[OSD([sQuery(id+"F7.wireOp",EDGE,"E24.left")])]});
            extrude(context, id + "F10", {"entities" : qUnion([Q0, Q1, Q2, Q3, Q4, Q5, Q6, Q7]), "operationType" : NewBodyOperationType.ADD, "endBound" : BoundingType.UP_TO_SURFACE, "oppositeDirection" : true, "depth" : 25 * mm, "endBoundEntityFace" : qUnion([Q8]), "offsetDistance" : 25 * mm});
        }
        {
            var Q0;
            Q0=makeQuery(id+"F8.opExtrude","SWEPT_FACE",FACE,{"disambiguationData":[OSD([sQuery(id+"F7.wireOp",EDGE,"E24.top")])]});
            var sketch = newSketch(context, id + "F11", { "sketchPlane" : qUnion([Q0])});
            skLineSegment(sketch, "E48", {"start": v(-470.81, 0) * mm, "end": v(-470.81, -75) * mm});
            skLineSegment(sketch, "E49", {"start": v(-470.81, -75) * mm, "end": v(-260, -75) * mm});
            skLineSegment(sketch, "E50", {"start": v(-470.81, 75) * mm, "end": v(-260, 75) * mm});
            skLineSegment(sketch, "E51", {"start": v(-470.81, 75) * mm, "end": v(-470.81, 0) * mm});
            skLineSegment(sketch, "E52", {"start": v(-260, 75) * mm, "end": v(-260, -75) * mm});
            skSolve(sketch);
        }
        {
            var Q0;
            Q0=makeQuery(id+"F11.imprint","IMPRINT",FACE,{"disambiguationData":[TD([[makeQuery(id+"F11.imprint","IMPRINT",EDGE,{"derivedFrom":sQuery(id+"F11.wireOp",EDGE,"E48")}),1.0]])]});
            var Q1;
            Q1=makeQuery(id+"F8.opExtrude","SWEPT_FACE",FACE,{"disambiguationData":[OSD([sQuery(id+"F7.wireOp",EDGE,"E25.bottom")])]});
            var Q2;
            Q2=makeQuery(id+"F4.opExtrude","SWEPT_BODY",BODY,{"disambiguationData":[OSD([sQuery(id+"F0.wireOp",EDGE,"E13.1.3"),sQuery(id+"F0.wireOp",EDGE,"E13.1.4"),sQuery(id+"F0.wireOp",EDGE,"E13.1.6"),sQuery(id+"F0.wireOp",EDGE,"E13.1.7"),sQuery(id+"F0.wireOp",EDGE,"E13.1.8"),sQuery(id+"F0.wireOp",EDGE,"E13.1.9")])]});
            extrude(context, id + "F12", {"entities" : qUnion([Q0]), "operationType" : NewBodyOperationType.REMOVE, "endBound" : BoundingType.UP_TO_SURFACE, "oppositeDirection" : true, "depth" : 25 * mm, "endBoundEntityFace" : qUnion([Q1]), "endBoundEntityBody" : qUnion([Q2]), "offsetDistance" : 25 * mm});
        }
        {
            var Q0;
            Q0=makeQuery(id+"F1.opExtrude","CAP_FACE",FACE,{"disambiguationData":[OSD([sQuery(id+"F0.wireOp",EDGE,"E0.bottom"),sQuery(id+"F0.wireOp",EDGE,"E0.left"),sQuery(id+"F0.wireOp",EDGE,"E0.right"),sQuery(id+"F0.wireOp",EDGE,"E1.0"),sQuery(id+"F0.wireOp",EDGE,"E1.1"),sQuery(id+"F0.wireOp",EDGE,"E1.2"),sQuery(id+"F0.wireOp",EDGE,"E1.3"),sQuery(id+"F0.wireOp",EDGE,"E2.filletArc"),sQuery(id+"F0.wireOp",EDGE,"E3.filletArc"),sQuery(id+"F0.wireOp",EDGE,"E4.filletArc"),sQuery(id+"F0.wireOp",EDGE,"E5.filletArc"),sQuery(id+"F0.wireOp",EDGE,"E6.filletArc"),sQuery(id+"F0.wireOp",EDGE,"E7.filletArc"),sQuery(id+"F0.wireOp",EDGE,"E8.filletArc"),sQuery(id+"F0.wireOp",EDGE,"E9.filletArc"),sQuery(id+"F0.wireOp",EDGE,"E12.bottom"),sQuery(id+"F0.wireOp",EDGE,"E18"),sQuery(id+"F0.wireOp",EDGE,"E19")])],"isStart":false});
            var sketch = newSketch(context, id + "F13", { "sketchPlane" : qUnion([Q0])});
            skLineSegment(sketch, "E53.0", {"start": v(144, -160) * mm, "end": v(-144, -160) * mm});
            skLineSegment(sketch, "E53.1", {"start": v(-144, 160) * mm, "end": v(144, 160) * mm});
            skLineSegment(sketch, "E54", {"start": v(0, -160) * mm, "end": v(-235.57, -568.01) * mm});
            skLineSegment(sketch, "E55", {"start": v(0, 160) * mm, "end": v(-235.57, 568.01) * mm});
            skLineSegment(sketch, "E56", {"start": v(-235.57, 568.01) * mm, "end": v(-192.26, 593.01) * mm});
            skLineSegment(sketch, "E57", {"start": v(-192.26, 593.01) * mm, "end": v(57.74, 160) * mm});
            skLineSegment(sketch, "E58", {"start": v(57.74, 160) * mm, "end": v(0, 160) * mm});
            skLineSegment(sketch, "E59", {"start": v(57.74, 160) * mm, "end": v(57.74, -160) * mm, "construction": true});
            skLineSegment(sketch, "E60", {"start": v(57.74, -160) * mm, "end": v(-192.26, -593.01) * mm});
            skLineSegment(sketch, "E61", {"start": v(-235.57, -568.01) * mm, "end": v(-192.26, -593.01) * mm});
            skLineSegment(sketch, "E62", {"start": v(-235.57, 568.01) * mm, "end": v(-235.57, -568.01) * mm, "construction": true});
            skSolve(sketch);
        }
        {
            var Q0;
            Q0=makeQuery(id+"F13.imprint","IMPRINT",FACE,{"disambiguationData":[TD([[makeQuery(id+"F13.imprint","IMPRINT",EDGE,{"derivedFrom":sQuery(id+"F13.wireOp",EDGE,"E55")}),-1.0]])]});
            var Q1;
            {var subQ0=sQuery(id+"F13.wireOp",EDGE,"E54");Q1=makeQuery(id+"F13.imprint","IMPRINT",FACE,{"disambiguationData":[TD([[makeQuery(id+"F13.imprint","IMPRINT",EDGE,{"derivedFrom":subQ0}),1.0]])]});}
            var Q2;
            Q2=makeQuery(id+"F8.opExtrude","SWEPT_FACE",FACE,{"disambiguationData":[OSD([sQuery(id+"F7.wireOp",EDGE,"E25.bottom")])]});
            extrude(context, id + "F14", {"entities" : qUnion([Q0, Q1]), "operationType" : NewBodyOperationType.ADD, "endBound" : BoundingType.UP_TO_SURFACE, "oppositeDirection" : true, "depth" : 25 * mm, "endBoundEntityFace" : qUnion([Q2]), "offsetDistance" : 25 * mm});
        }
    });
